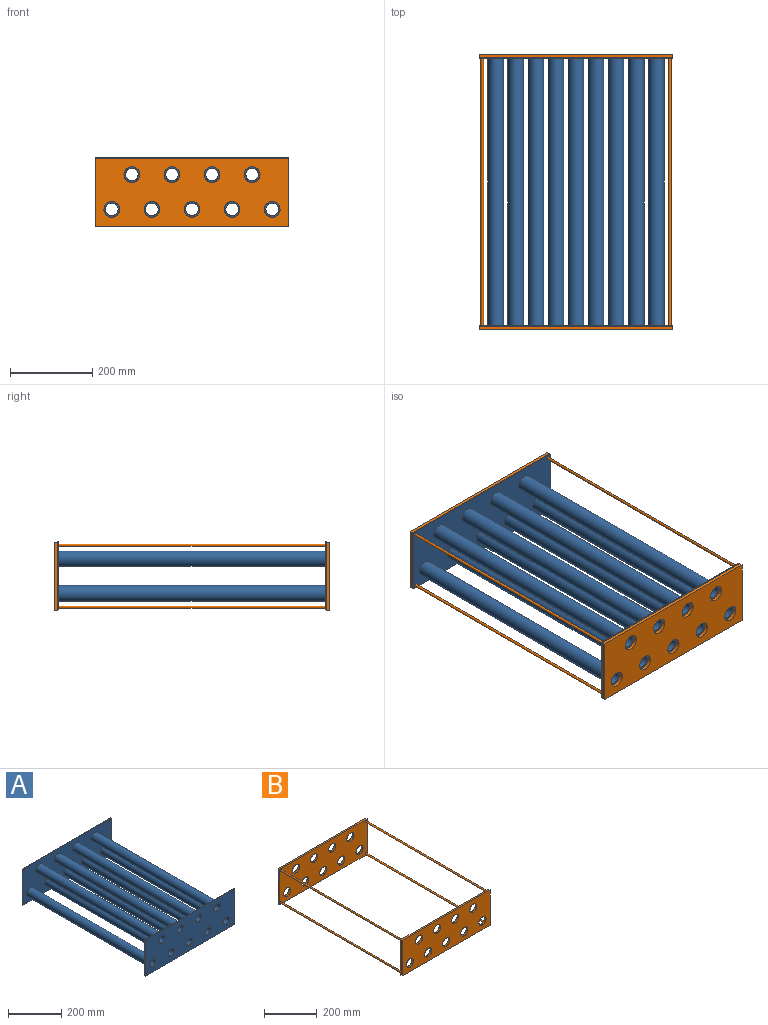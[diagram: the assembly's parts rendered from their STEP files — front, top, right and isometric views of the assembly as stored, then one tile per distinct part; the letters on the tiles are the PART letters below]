
ASSEMBLY  parts=2 mates=1
PART A: 38 faces, bbox 469.9x652x165.1 mm
  f0: cylinder r=19.05mm len=646.94mm, axis (0,-1,0), area 77435mm2, adj f28,f37
  f1: plane 469.9x165.1mm, normal (0,1,0), area 70886.9mm2, adj f2,f5,f7,f9,f11,f13,f15,f17
  f2: cylinder r=15.24mm len=652.02mm, axis (0,-1,0), area 62434.5mm2, adj f1,f3
  f3: plane 469.9x165.1mm, normal (0,-1,0), area 70886.9mm2, adj f2,f5,f7,f9,f11,f13,f15,f17
  f4: cylinder r=19.05mm len=646.94mm, axis (0,-1,0), area 77435mm2, adj f28,f37
  f5: cylinder r=15.24mm len=652.02mm, axis (0,-1,0), area 62434.5mm2, adj f1,f3
  f6: cylinder r=19.05mm len=646.94mm, axis (0,-1,0), area 77435mm2, adj f28,f37
  f7: cylinder r=15.24mm len=652.02mm, axis (0,-1,0), area 62434.5mm2, adj f1,f3
  f8: cylinder r=19.05mm len=646.94mm, axis (0,-1,0), area 77435mm2, adj f28,f37
  f9: cylinder r=15.24mm len=652.02mm, axis (0,-1,0), area 62434.5mm2, adj f1,f3
  f10: cylinder r=19.05mm len=646.94mm, axis (0,-1,0), area 77435mm2, adj f28,f37
  f11: cylinder r=15.24mm len=652.02mm, axis (0,-1,0), area 62434.5mm2, adj f1,f3
  f12: cylinder r=19.05mm len=646.94mm, axis (0,-1,0), area 77435mm2, adj f28,f37
  f13: cylinder r=15.24mm len=652.02mm, axis (0,-1,0), area 62434.5mm2, adj f1,f3
  f14: cylinder r=19.05mm len=646.94mm, axis (0,-1,0), area 77435mm2, adj f28,f37
  f15: cylinder r=15.24mm len=652.02mm, axis (0,-1,0), area 62434.5mm2, adj f1,f3
  f16: cylinder r=19.05mm len=646.94mm, axis (0,-1,0), area 77435mm2, adj f28,f37
  f17: cylinder r=15.24mm len=652.02mm, axis (0,-1,0), area 62434.5mm2, adj f1,f3
  f18: cylinder r=19.05mm len=646.94mm, axis (0,-1,0), area 77435mm2, adj f28,f37
  f19: cylinder r=15.24mm len=652.02mm, axis (0,-1,0), area 62434.5mm2, adj f1,f3
  f20: plane 165.1x2.54mm, normal (-1,0,0), area 419.4mm2, adj f3,f21,f27,f28
  f21: plane 469.9x2.54mm, normal (0,0,-1), area 1193.5mm2, adj f3,f20,f22,f28
  f22: plane 165.1x2.54mm, normal (1,0,0), area 419.4mm2, adj f3,f21,f27,f28
  f23: cylinder r=3.17mm len=6.35mm, axis (0,-1,0), area 50.7mm2, adj f3,f28
  f24: cylinder r=3.17mm len=6.35mm, axis (0,-1,0), area 50.7mm2, adj f3,f28
  f25: cylinder r=3.17mm len=6.35mm, axis (0,-1,0), area 50.7mm2, adj f3,f28
  f26: cylinder r=3.17mm len=6.35mm, axis (0,-1,0), area 50.7mm2, adj f3,f28
  f27: plane 469.9x2.54mm, normal (0,0,1), area 1193.5mm2, adj f3,f20,f22,f28
  f28: plane 469.9x165.1mm, normal (0,1,0), area 67193mm2, adj f0,f4,f6,f8,f10,f12,f14,f16
  f29: plane 165.1x2.54mm, normal (-1,0,0), area 419.4mm2, adj f1,f30,f36,f37
  f30: plane 469.9x2.54mm, normal (0,0,-1), area 1193.5mm2, adj f1,f29,f31,f37
  f31: plane 165.1x2.54mm, normal (1,0,0), area 419.4mm2, adj f1,f30,f36,f37
  f32: cylinder r=3.17mm len=6.35mm, axis (0,1,0), area 50.7mm2, adj f1,f37
  f33: cylinder r=3.17mm len=6.35mm, axis (0,1,0), area 50.7mm2, adj f1,f37
  f34: cylinder r=3.17mm len=6.35mm, axis (0,1,0), area 50.7mm2, adj f1,f37
  f35: cylinder r=3.17mm len=6.35mm, axis (0,1,0), area 50.7mm2, adj f1,f37
  f36: plane 469.9x2.54mm, normal (0,0,1), area 1193.5mm2, adj f1,f29,f31,f37
  f37: plane 469.9x165.1mm, normal (0,-1,0), area 67193mm2, adj f0,f4,f6,f8,f10,f12,f14,f16
PART B: 34 faces, bbox 469.9x668.8x165.1 mm
  f0: plane 165.1x8.38mm, normal (-1,0,0), area 1383.9mm2, adj f1,f11,f13,f14
  f1: plane 469.9x8.38mm, normal (0,0,-1), area 3938.7mm2, adj f0,f2,f13,f14
  f2: plane 165.1x8.38mm, normal (1,0,0), area 1383.9mm2, adj f1,f11,f13,f14
  f3: cylinder r=19.05mm len=38.1mm, axis (0,1,0), area 1003.3mm2, adj f13,f14
  f4: cylinder r=19.05mm len=38.1mm, axis (0,1,0), area 1003.3mm2, adj f13,f14
  f5: cylinder r=19.05mm len=38.1mm, axis (0,1,0), area 1003.3mm2, adj f13,f14
  f6: cylinder r=19.05mm len=38.1mm, axis (0,1,0), area 1003.3mm2, adj f13,f14
  f7: cylinder r=19.05mm len=38.1mm, axis (0,1,0), area 1003.3mm2, adj f13,f14
  f8: cylinder r=19.05mm len=38.1mm, axis (0,1,0), area 1003.3mm2, adj f13,f14
  f9: cylinder r=19.05mm len=38.1mm, axis (0,1,0), area 1003.3mm2, adj f13,f14
  f10: cylinder r=19.05mm len=38.1mm, axis (0,1,0), area 1003.3mm2, adj f13,f14
  f11: plane 469.9x8.38mm, normal (0,0,1), area 3938.7mm2, adj f0,f2,f13,f14
  f12: cylinder r=19.05mm len=38.1mm, axis (0,1,0), area 1003.3mm2, adj f13,f14
  f13: plane 469.9x165.1mm, normal (0,-1,0), area 67319.7mm2, adj f0,f1,f2,f3,f4,f5,f6,f7
  f14: plane 469.9x165.1mm, normal (0,1,0), area 67193mm2, adj f0,f1,f2,f3,f4,f5,f6,f7
  f15: plane 469.9x165.1mm, normal (0,1,0), area 67319.7mm2, adj f17,f18,f19,f20,f21,f22,f23,f24
  f16: plane 469.9x165.1mm, normal (0,-1,0), area 67193mm2, adj f17,f18,f19,f20,f21,f22,f23,f24
  f17: cylinder r=19.05mm len=38.1mm, axis (0,1,0), area 1003.3mm2, adj f15,f16
  f18: plane 469.9x8.38mm, normal (0,0,1), area 3938.7mm2, adj f15,f16,f27,f29
  f19: cylinder r=19.05mm len=38.1mm, axis (0,1,0), area 1003.3mm2, adj f15,f16
  f20: cylinder r=19.05mm len=38.1mm, axis (0,1,0), area 1003.3mm2, adj f15,f16
  f21: cylinder r=19.05mm len=38.1mm, axis (0,1,0), area 1003.3mm2, adj f15,f16
  f22: cylinder r=19.05mm len=38.1mm, axis (0,1,0), area 1003.3mm2, adj f15,f16
  f23: cylinder r=19.05mm len=38.1mm, axis (0,1,0), area 1003.3mm2, adj f15,f16
  f24: cylinder r=19.05mm len=38.1mm, axis (0,1,0), area 1003.3mm2, adj f15,f16
  f25: cylinder r=19.05mm len=38.1mm, axis (0,1,0), area 1003.3mm2, adj f15,f16
  f26: cylinder r=19.05mm len=38.1mm, axis (0,1,0), area 1003.3mm2, adj f15,f16
  f27: plane 165.1x8.38mm, normal (1,0,0), area 1383.9mm2, adj f15,f16,f18,f28
  f28: plane 469.9x8.38mm, normal (0,0,-1), area 3938.7mm2, adj f15,f16,f27,f29
  f29: plane 165.1x8.38mm, normal (-1,0,0), area 1383.9mm2, adj f15,f16,f18,f28
  f30: cylinder r=3.17mm len=652.02mm, axis (0,-1,0), area 13007.2mm2, adj f14,f16
  f31: cylinder r=3.17mm len=652.02mm, axis (0,-1,0), area 13007.2mm2, adj f14,f16
  f32: cylinder r=3.17mm len=652.02mm, axis (0,-1,0), area 13007.2mm2, adj f14,f16
  f33: cylinder r=3.17mm len=652.02mm, axis (0,-1,0), area 13007.2mm2, adj f14,f16
PLACE A t=(29.8,19.92,4.08)mm
PLACE B t=(29.8,19.92,3.79)mm
MATE fastened B.f16 <-> A.f1  axis (0,-1,0) through (-60.01,671.94,-440.9)mm
